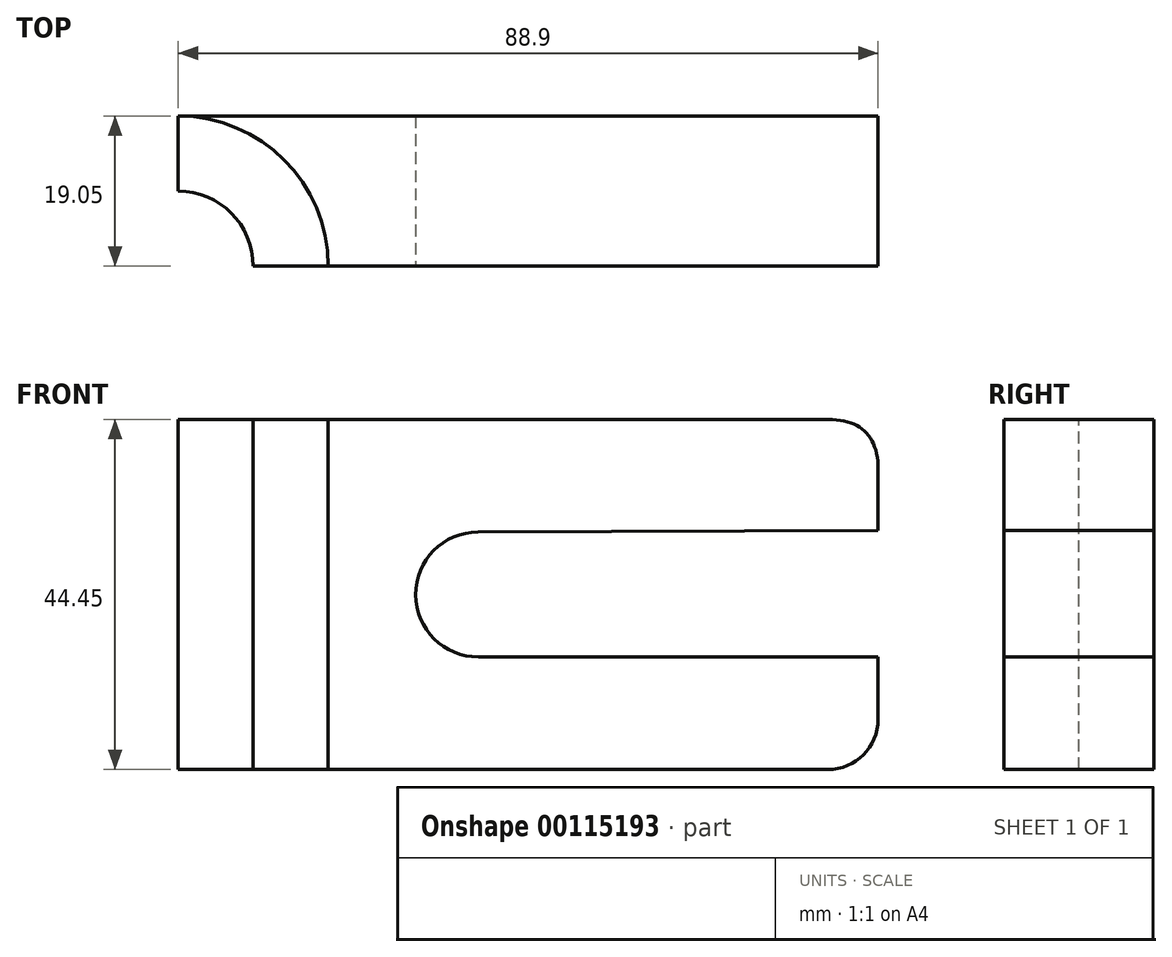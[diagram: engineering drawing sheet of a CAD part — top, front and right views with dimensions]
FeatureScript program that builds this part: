
annotation { "Feature Type Name" : "Feature", "Feature Type Description" : "" }
export const myFeature = defineFeature(function(context is Context, id is Id, definition is map)
    precondition{}
    {
        {
            var Q0;
            Q0=qCreatedBy(makeId("Top.planeOp"),FACE);
            var sketch = newSketch(context, id + "F0", { "sketchPlane" : qUnion([Q0])});
            skCircle(sketch, "E0", {"center": v(0, 0) * mm, "radius": 19.05 * mm});
            skSolve(sketch);
        }
        {
            var Q0;
            Q0=makeQuery(id+"F0.imprint","IMPRINT",FACE,{"disambiguationData":[TD([[makeQuery(id+"F0.imprint","IMPRINT",EDGE,{"derivedFrom":sQuery(id+"F0.wireOp",EDGE,"E0")}),1.0]])]});
            extrude(context, id + "F1", {"entities" : qUnion([Q0]), "depth" : 44.45 * mm});
        }
        {
            var Q0;
            Q0=makeQuery(id+"F1.opExtrude","CAP_FACE",FACE,{"disambiguationData":[OSD([sQuery(id+"F0.wireOp",EDGE,"E0")])],"isStart":false});
            var sketch = newSketch(context, id + "F2", { "sketchPlane" : qUnion([Q0])});
            skCircle(sketch, "E1", {"center": v(0, 0) * mm, "radius": 9.53 * mm});
            skSolve(sketch);
        }
        {
            var Q0;
            Q0=makeQuery(id+"F2.imprint","IMPRINT",FACE,{"disambiguationData":[TD([[makeQuery(id+"F2.imprint","IMPRINT",EDGE,{"derivedFrom":sQuery(id+"F2.wireOp",EDGE,"E1")}),1.0]])]});
            extrude(context, id + "F3", {"entities" : qUnion([Q0]), "operationType" : NewBodyOperationType.REMOVE, "oppositeDirection" : true, "depth" : 81.1 * mm});
        }
        {
            var Q0;
            Q0=makeQuery(id+"F1.opExtrude","CAP_FACE",FACE,{"disambiguationData":[OSD([sQuery(id+"F0.wireOp",EDGE,"E0")])],"isStart":false});
            var sketch = newSketch(context, id + "F4", { "sketchPlane" : qUnion([Q0])});
            skLineSegment(sketch, "E2", {"start": v(0, 19.05) * mm, "end": v(88.9, 19.05) * mm});
            skLineSegment(sketch, "E3", {"start": v(0, -19.05) * mm, "end": v(88.9, -19.05) * mm});
            skLineSegment(sketch, "E4", {"start": v(88.9, -19.05) * mm, "end": v(88.9, 19.05) * mm});
            skSolve(sketch);
        }
        {
            var Q0;
            Q0=makeQuery(id+"F1.opExtrude","CAP_FACE",FACE,{"disambiguationData":[OSD([sQuery(id+"F0.wireOp",EDGE,"E0")])],"isStart":true});
            var sketch = newSketch(context, id + "F5", { "sketchPlane" : qUnion([Q0])});
            skLineSegment(sketch, "E5", {"start": v(0, 19.05) * mm, "end": v(88.9, 19.05) * mm});
            skLineSegment(sketch, "E6", {"start": v(88.9, 19.05) * mm, "end": v(88.9, -19.05) * mm});
            skLineSegment(sketch, "E7", {"start": v(88.9, -19.05) * mm, "end": v(0, -19.05) * mm});
            skSolve(sketch);
        }
        {
            var Q0;
            {var subQ0=sQuery(id+"F5.wireOp",EDGE,"E5");Q0=makeQuery(id+"F5.imprint","IMPRINT",FACE,{"disambiguationData":[TD([[makeQuery(id+"F5.imprint","IMPRINT",EDGE,{"derivedFrom":subQ0}),-1.0]])]});}
            extrude(context, id + "F6", {"entities" : qUnion([Q0]), "oppositeDirection" : true, "depth" : 44.45 * mm});
        }
        {
            var Q0;
            Q0=makeQuery(id+"F6.opExtrude","SWEPT_EDGE",EDGE,{"disambiguationData":[OSD([sQuery(id+"F0.wireOp",EDGE,"E0"),sQuery(id+"F5.wireOp",EDGE,"E5")])]});
            fillet(context, id + "F7", {"entities" : qUnion([Q0]), "radius" : 6.35 * mm, "tangentPropagation" : true, "allowEdgeOverflow" : false});
        }
        {
            var Q0;
            Q0=makeQuery(id+"F6.opExtrude","CAP_EDGE",EDGE,{"disambiguationData":[OSD([sQuery(id+"F5.wireOp",EDGE,"E6")])],"isStart":true});
            fillet(context, id + "F8", {"entities" : qUnion([Q0]), "radius" : 6.35 * mm, "tangentPropagation" : true, "allowEdgeOverflow" : false});
        }
        {
            var Q0;
            Q0=makeQuery(id+"F6.opExtrude","CAP_EDGE",EDGE,{"disambiguationData":[OSD([sQuery(id+"F5.wireOp",EDGE,"E6")])],"isStart":false});
            fillet(context, id + "F9", {"entities" : qUnion([Q0]), "radius" : 6.35 * mm, "rho" : 0.5, "crossSection" : FilletCrossSection.CONIC, "allowEdgeOverflow" : false});
        }
        {
            var Q0;
            Q0=makeQuery(id+"F6.opExtrude","SWEPT_FACE",FACE,{"disambiguationData":[OSD([sQuery(id+"F5.wireOp",EDGE,"E5")])]});
            var sketch = newSketch(context, id + "F10", { "sketchPlane" : qUnion([Q0])});
            skCircle(sketch, "E8", {"center": v(38.1, 22.22) * mm, "radius": 7.94 * mm});
            skSolve(sketch);
        }
        {
            var Q0;
            Q0=makeQuery(id+"F10.imprint","IMPRINT",FACE,{"disambiguationData":[TD([[makeQuery(id+"F10.imprint","IMPRINT",EDGE,{"derivedFrom":sQuery(id+"F10.wireOp",EDGE,"E8")}),1.0]])]});
            extrude(context, id + "F11", {"entities" : qUnion([Q0]), "operationType" : NewBodyOperationType.REMOVE, "oppositeDirection" : true, "depth" : 103.37 * mm});
        }
        {
            var Q0;
            Q0=makeQuery(id+"F6.opExtrude","SWEPT_FACE",FACE,{"disambiguationData":[OSD([sQuery(id+"F5.wireOp",EDGE,"E5")])]});
            var sketch = newSketch(context, id + "F12", { "sketchPlane" : qUnion([Q0])});
            skLineSegment(sketch, "E9", {"start": v(38.07, 14.29) * mm, "end": v(88.9, 14.29) * mm});
            skLineSegment(sketch, "E10", {"start": v(38.07, 30.16) * mm, "end": v(88.9, 30.38) * mm});
            skSolve(sketch);
        }
        {
            var Q0;
            {var subQ5=sQuery(id+"F12.wireOp",EDGE,"E10");Q0=makeQuery(id+"F12.imprint","IMPRINT",FACE,{"disambiguationData":[TD([[makeQuery(id+"F12.imprint","IMPRINT",EDGE,{"derivedFrom":subQ5}),-1.0]])]});}
            extrude(context, id + "F13", {"entities" : qUnion([Q0]), "operationType" : NewBodyOperationType.REMOVE, "oppositeDirection" : true, "depth" : 79.13 * mm});
        }
        {
            var Q0;
            {var subQ0=sQuery(id+"F4.wireOp",EDGE,"E2");Q0=makeQuery(id+"F4.imprint","IMPRINT",FACE,{"disambiguationData":[TD([[makeQuery(id+"F4.imprint","IMPRINT",EDGE,{"derivedFrom":subQ0}),-1.0]])]});}
            var sketch = newSketch(context, id + "F14", { "sketchPlane" : qUnion([Q0])});
            skSolve(sketch);
        }
        {
            var Q0;
            Q0 = qSketchRegion(id + "F14", true);
            var Q1;
            Q1=makeQuery(id+"F6.opExtrude","SWEPT_FACE",FACE,{"disambiguationData":[OSD([sQuery(id+"F5.wireOp",EDGE,"E5")])]});
            extrude(context, id + "F15", {"entities" : qUnion([Q0, Q1]), "operationType" : NewBodyOperationType.ADD, "oppositeDirection" : true, "depth" : 38.1 * mm});
        }
        {
            var Q0;
            Q0=makeQuery(id+"F6.opExtrude","SWEPT_FACE",FACE,{"disambiguationData":[OSD([sQuery(id+"F5.wireOp",EDGE,"E5")])]});
            extrude(context, id + "F16", {"entities" : qUnion([Q0]), "operationType" : NewBodyOperationType.ADD, "oppositeDirection" : true, "depth" : 25.4 * mm});
        }
        {
            var Q0;
            Q0=makeQuery(id+"F6.opExtrude","SWEPT_FACE",FACE,{"disambiguationData":[OSD([sQuery(id+"F5.wireOp",EDGE,"E7")])]});
            extrude(context, id + "F17", {"entities" : qUnion([Q0]), "operationType" : NewBodyOperationType.INTERSECT, "oppositeDirection" : true, "depth" : 19.05 * mm});
        }
    });
